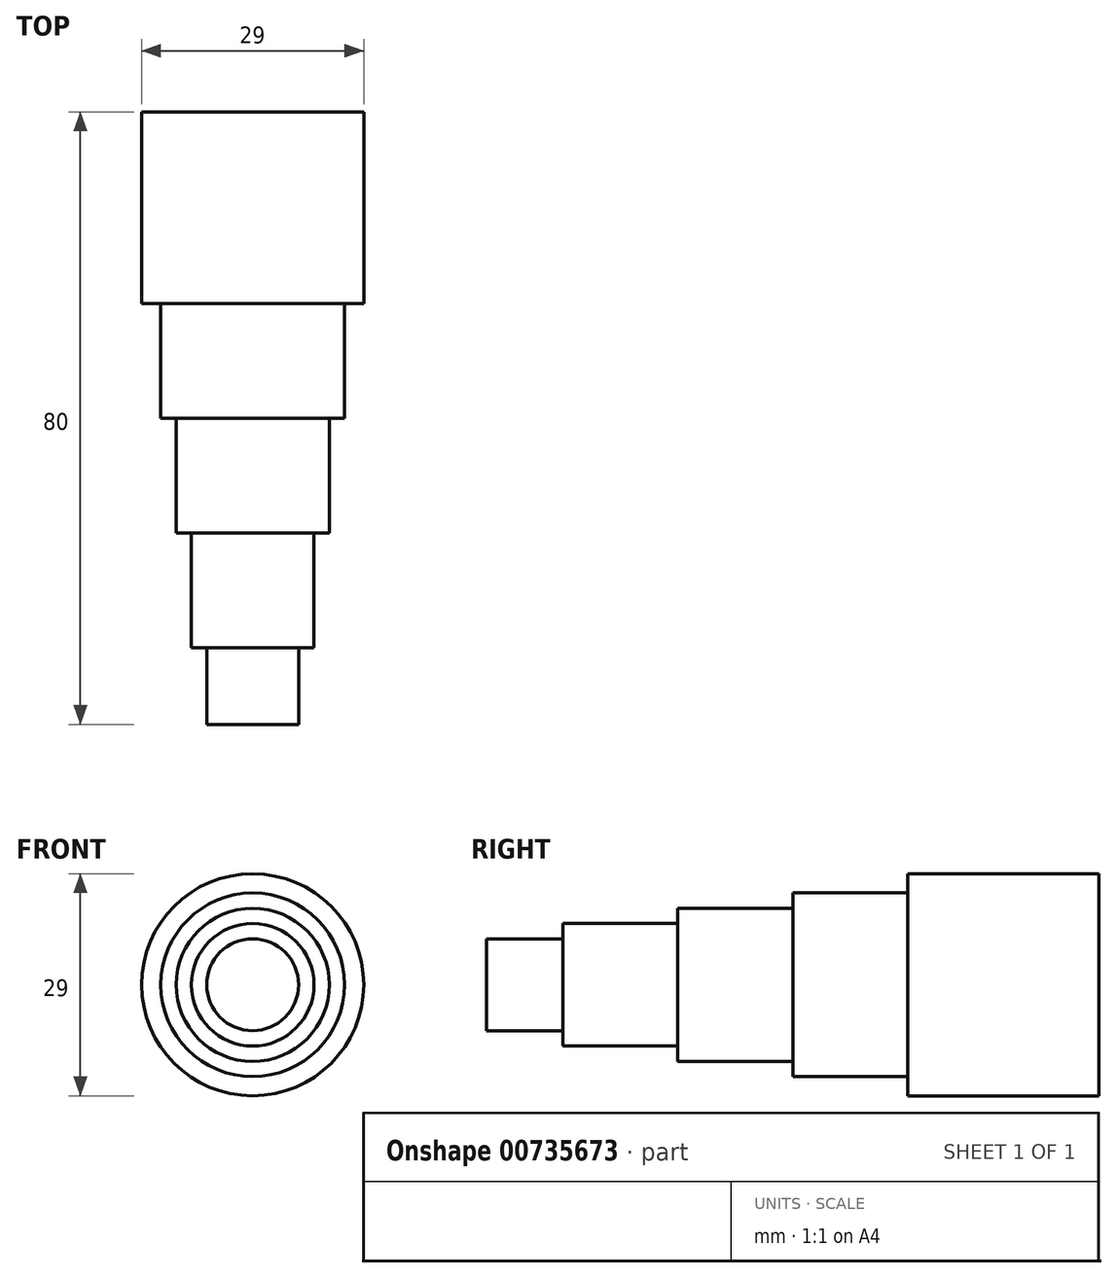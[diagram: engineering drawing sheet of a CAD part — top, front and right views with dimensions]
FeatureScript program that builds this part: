
annotation { "Feature Type Name" : "Feature", "Feature Type Description" : "" }
export const myFeature = defineFeature(function(context is Context, id is Id, definition is map)
    precondition{}
    {
        {
            var Q0;
            Q0=qCreatedBy(makeId("Top.planeOp"),FACE);
            var sketch = newSketch(context, id + "F0", { "sketchPlane" : qUnion([Q0])});
            skLineSegment(sketch, "E0", {"start": v(0, 0) * mm, "end": v(6, 0) * mm});
            skLineSegment(sketch, "E1", {"start": v(6, 0) * mm, "end": v(6, 10) * mm});
            skLineSegment(sketch, "E2", {"start": v(8, 10) * mm, "end": v(6, 10) * mm});
            skLineSegment(sketch, "E3", {"start": v(8, 10) * mm, "end": v(8, 25) * mm});
            skLineSegment(sketch, "E4", {"start": v(8, 25) * mm, "end": v(10, 25) * mm});
            skLineSegment(sketch, "E5", {"start": v(10, 40) * mm, "end": v(10, 25) * mm});
            skLineSegment(sketch, "E6", {"start": v(10, 40) * mm, "end": v(12, 40) * mm});
            skLineSegment(sketch, "E7", {"start": v(12, 40) * mm, "end": v(12, 55) * mm});
            skLineSegment(sketch, "E8", {"start": v(12, 55) * mm, "end": v(14.5, 55) * mm});
            skLineSegment(sketch, "E9", {"start": v(14.5, 55) * mm, "end": v(14.5, 80) * mm});
            skLineSegment(sketch, "E10", {"start": v(14.5, 80) * mm, "end": v(0, 80) * mm});
            skLineSegment(sketch, "E11", {"start": v(0, 80) * mm, "end": v(0, 0) * mm});
            skSolve(sketch);
        }
        {
            var Q0;
            Q0 = qSketchRegion(id + "F0", true);
            var Q1;
            Q1=sQuery(id+"F0.wireOp",EDGE,"E11");
            revolve(context, id + "F1", {"surfaceOperationType" : NewSurfaceOperationType.NEW, "entities" : qUnion([Q0]), "axis" : qUnion([Q1]), "revolveType" : RevolveType.FULL});
        }
    });
